# Revit family: CRTW2X2
name_source: partatom
category: Lighting Fixtures
units: mm (PartAtom-declared; Revit-internal decimal feet)

## family parameters
Always vertical = Yes
Cut with Voids When Loaded = No
Host = Ceiling
Light Source = Yes
OmniClass Number = 23.80.70.11
OmniClass Title = Luminaries for Internal Lighting
Part Type = Normal
Room Calculation Point = No
Round Connector Dimension = Use Diameter
Shared = No

## types (1)
- CRTWo2X2-LED840K070LUNV-P56P73
    Apparent Load = 51 VA
    Color Filter = 16777215
    Description = LED Recessed Cleanroom Top Access Walkable with Overlapping Door Frame
    Dimming Lamp Color Temperature Shift = <None>
    Emit Shape Visible in Rendering = No
    Emit from Rectangle Length = 2' - 3 3/32"
    Emit from Rectangle Width = 2' - 3 3/32"
    Housing Finish = <By Category>
    Lamp = LED
    Lamp Wattage = 51 VA
    Length = 2' - 3 3/32"
    Lens Finish = <By Category>
    Manufacturer = Certolux
    Model = CRTW
    Photometric Web File = CRTWO-2X2-LED840K070LUNV-P56P73.IES
    Tilt Angle = 90.00°
    URL = https://www.viscor.com
    Voltage = 120 V
    Width = 2' - 3 3/32"

## geometry (parser evidence)
native form markers: Sweep x3
no freeform markers — native parametric forms only
